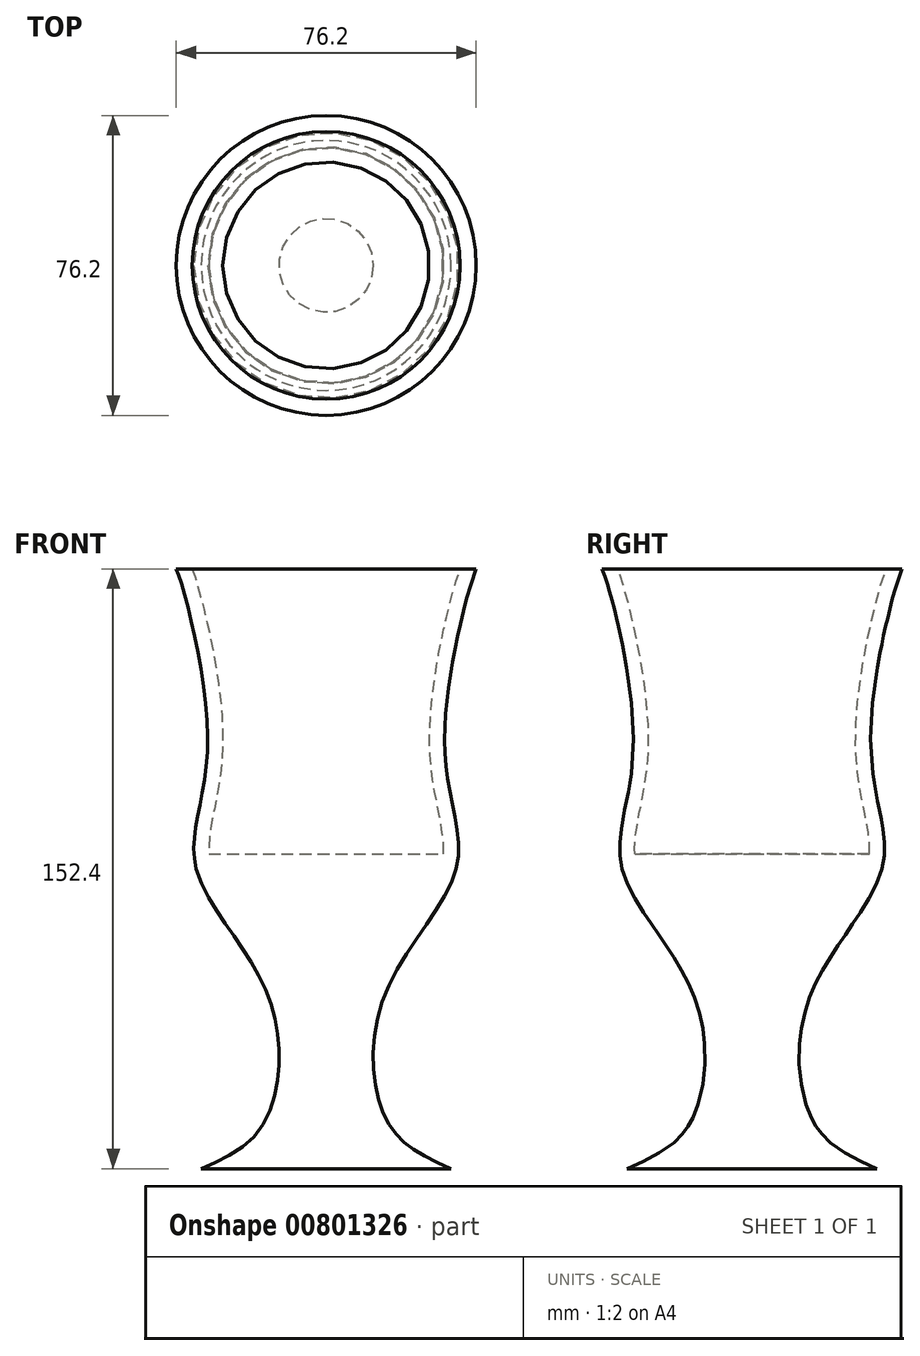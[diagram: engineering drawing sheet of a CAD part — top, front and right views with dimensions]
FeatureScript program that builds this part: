
annotation { "Feature Type Name" : "Feature", "Feature Type Description" : "" }
export const myFeature = defineFeature(function(context is Context, id is Id, definition is map)
    precondition{}
    {
        {
            var Q0;
            Q0=qCreatedBy(makeId("Front.planeOp"),FACE);
            var sketch = newSketch(context, id + "F0", { "sketchPlane" : qUnion([Q0])});
            skLineSegment(sketch, "E0", {"start": v(-3, 30.58) * mm, "end": v(-3, -45.62) * mm});
            skLineSegment(sketch, "E1", {"start": v(-3, 30.58) * mm, "end": v(-3, 106.78) * mm});
            skLineSegment(sketch, "E2", {"start": v(-3, -45.62) * mm, "end": v(28.75, -45.62) * mm});
            skLineSegment(sketch, "E3", {"start": v(-3, 106.78) * mm, "end": v(35.1, 106.78) * mm});
            skFitSpline(sketch, "E4", {"points": [v(35.1, 106.78) * mm, v(27.1, 61.9) * mm, v(30.02, 30.58) * mm, v(11.85, -1.5) * mm, v(12.27, -33.08) * mm, v(28.75, -45.62) * mm], "startDerivative": vector(-27.4, -65.87) * mm, "endDerivative": vector(156, -66.86) * mm});
            skLineSegment(sketch, "E5", {"start": v(-3, 30.58) * mm, "end": v(30.02, 30.58) * mm});
            skSolve(sketch);
        }
        {
            var Q0;
            Q0=makeQuery(id+"F0.imprint","IMPRINT",FACE,{"disambiguationData":[TD([[makeQuery(id+"F0.imprint","IMPRINT",EDGE,{"derivedFrom":sQuery(id+"F0.wireOp",EDGE,"E1")}),-1.0]])]});
            var Q1;
            Q1=sQuery(id+"F0.wireOp",EDGE,"E1");
            revolve(context, id + "F1", {"surfaceOperationType" : NewSurfaceOperationType.NEW, "entities" : qUnion([Q0]), "axis" : qUnion([Q1]), "revolveType" : RevolveType.FULL});
        }
        {
            var Q0;
            Q0=makeQuery(id+"F1.opRevolve","SWEPT_FACE",FACE,{"disambiguationData":[OSD([sQuery(id+"F0.wireOp",EDGE,"E3")])]});
            shell(context, id + "F2", {"entities" : qUnion([Q0]), "thickness" : 3.8 * mm});
        }
        {
            var Q0;
            Q0=makeQuery(id+"F0.imprint","IMPRINT",FACE,{"disambiguationData":[TD([[makeQuery(id+"F0.imprint","IMPRINT",EDGE,{"derivedFrom":sQuery(id+"F0.wireOp",EDGE,"E0")}),1.0]])]});
            var Q1;
            Q1=sQuery(id+"F0.wireOp",EDGE,"E0");
            revolve(context, id + "F3", {"operationType" : NewBodyOperationType.ADD, "surfaceOperationType" : NewSurfaceOperationType.NEW, "entities" : qUnion([Q0]), "axis" : qUnion([Q1]), "revolveType" : RevolveType.FULL});
        }
    });
